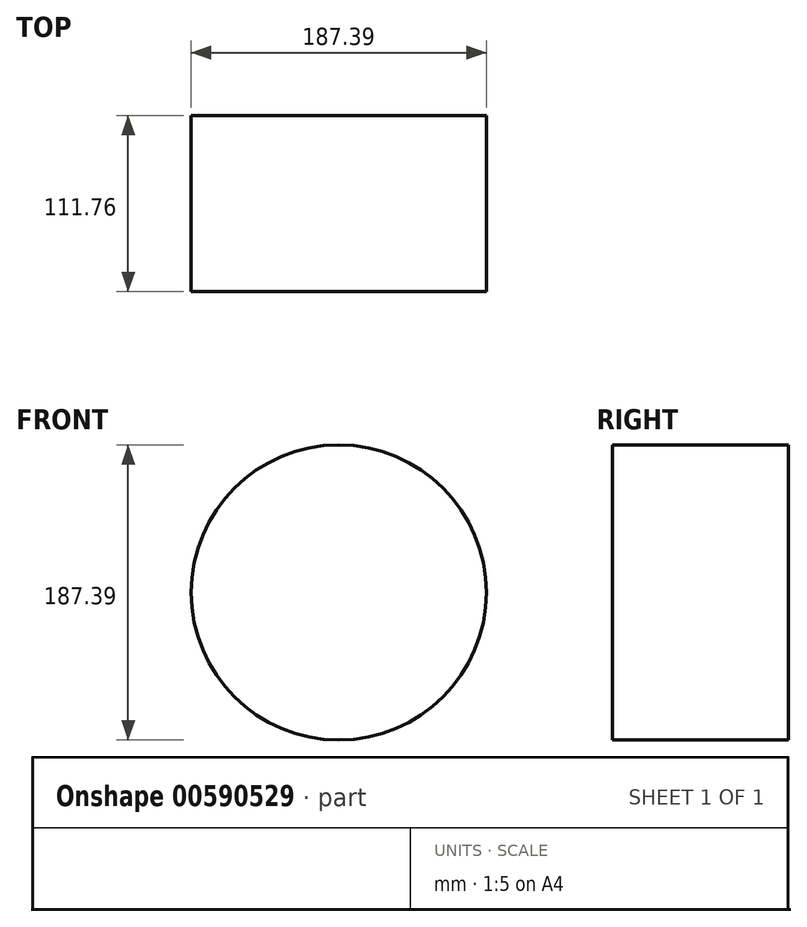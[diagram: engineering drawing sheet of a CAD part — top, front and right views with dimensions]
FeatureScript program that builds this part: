
annotation { "Feature Type Name" : "Feature", "Feature Type Description" : "" }
export const myFeature = defineFeature(function(context is Context, id is Id, definition is map)
    precondition{}
    {
        {
            var Q0;
            Q0=qCreatedBy(makeId("Front.planeOp"),FACE);
            var sketch = newSketch(context, id + "F0", { "sketchPlane" : qUnion([Q0])});
            skCircle(sketch, "E0", {"center": v(-35.15, 39.25) * mm, "radius": 93.7 * mm});
            skLineSegment(sketch, "E1", {"start": v(-31.81, 106.6) * mm, "end": v(-12.9, 59.3) * mm});
            skLineSegment(sketch, "E2", {"start": v(-65.68, 89.02) * mm, "end": v(-42.57, 39.76) * mm});
            skArc(sketch, "E3", {"start": v(-52.46, 4.23) * mm, "mid": v(-13.98, 5.51) * mm, "end": v(8.29, 36.91) * mm});
            skSolve(sketch);
        }
        {
            var Q0;
            Q0=makeQuery(id+"F0.imprint","IMPRINT",FACE,{"disambiguationData":[TD([[makeQuery(id+"F0.imprint","IMPRINT",EDGE,{"derivedFrom":sQuery(id+"F0.wireOp",EDGE,"E0")}),1.0]])]});
            extrude(context, id + "F1", {"entities" : qUnion([Q0]), "oppositeDirection" : true, "depth" : 111.76 * mm, "offsetDistance" : 25.4 * mm});
        }
    });
